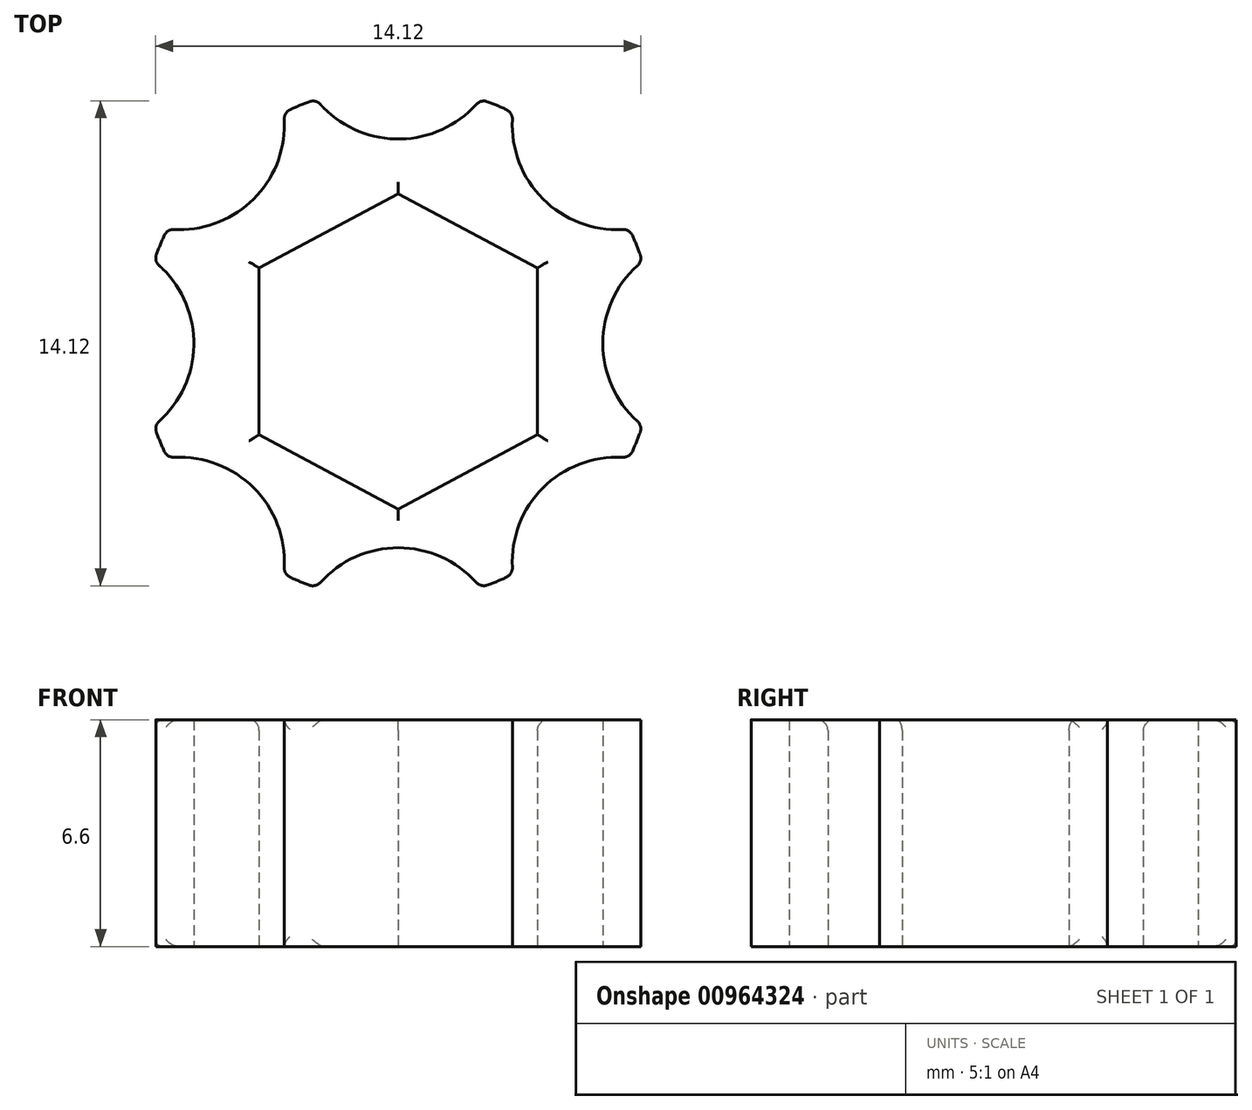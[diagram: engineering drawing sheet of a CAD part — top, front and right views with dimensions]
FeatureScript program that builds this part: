
annotation { "Feature Type Name" : "Feature", "Feature Type Description" : "" }
export const myFeature = defineFeature(function(context is Context, id is Id, definition is map)
    precondition{}
    {
        {
            var Q0;
            Q0=qCreatedBy(makeId("Top.planeOp"),FACE);
            var sketch = newSketch(context, id + "F0", { "sketchPlane" : qUnion([Q0])});
            skLineSegment(sketch, "E0", {"start": v(-4.05, 2.2) * mm, "end": v(-4.05, -2.66) * mm});
            skLineSegment(sketch, "E1", {"start": v(-4.05, -2.66) * mm, "end": v(0, -4.82) * mm});
            skLineSegment(sketch, "E2", {"start": v(0, -4.82) * mm, "end": v(4.05, -2.66) * mm});
            skLineSegment(sketch, "E3", {"start": v(4.05, -2.66) * mm, "end": v(4.05, 2.2) * mm});
            skLineSegment(sketch, "E4", {"start": v(4.05, 2.2) * mm, "end": v(0, 4.36) * mm});
            skLineSegment(sketch, "E5", {"start": v(0, 4.36) * mm, "end": v(-4.05, 2.2) * mm});
            skCircle(sketch, "E6", {"center": v(0, 0) * mm, "radius": 7.5 * mm});
            skLineSegment(sketch, "E7", {"start": v(0, 9) * mm, "end": v(0, 0) * mm, "construction": true});
            skCircle(sketch, "E8", {"center": v(0, 9) * mm, "radius": 3.05 * mm});
            skCircle(sketch, "E9.1.0", {"center": v(-6.36, 6.36) * mm, "radius": 3.05 * mm});
            skCircle(sketch, "E9.2.0", {"center": v(-9, 0) * mm, "radius": 3.05 * mm});
            skCircle(sketch, "E9.3.0", {"center": v(-6.36, -6.36) * mm, "radius": 3.05 * mm});
            skCircle(sketch, "E9.4.0", {"center": v(0, -9) * mm, "radius": 3.05 * mm});
            skCircle(sketch, "E9.5.0", {"center": v(6.36, -6.36) * mm, "radius": 3.05 * mm});
            skCircle(sketch, "E9.6.0", {"center": v(9, 0) * mm, "radius": 3.05 * mm});
            skCircle(sketch, "E9.7.0", {"center": v(6.36, 6.36) * mm, "radius": 3.05 * mm});
            skSolve(sketch);
        }
        {
            var Q0;
            Q0=makeQuery(id+"F0.imprint","IMPRINT",FACE,{"disambiguationData":[TD([[makeQuery(id+"F0.imprint","IMPRINT",EDGE,{"derivedFrom":sQuery(id+"F0.wireOp",EDGE,"E0")}),-1.0]])]});
            extrude(context, id + "F1", {"entities" : qUnion([Q0]), "depth" : 6.6 * mm, "offsetDistance" : 25 * mm});
        }
        {
            var Q0;
            Q0=makeQuery(id+"F1.opExtrude","CAP_EDGE",EDGE,{"disambiguationData":[OSD([sQuery(id+"F0.wireOp",EDGE,"E5")])],"isStart":false});
            var Q1;
            Q1=makeQuery(id+"F1.opExtrude","CAP_EDGE",EDGE,{"disambiguationData":[OSD([sQuery(id+"F0.wireOp",EDGE,"E0")])],"isStart":false});
            var Q2;
            Q2=makeQuery(id+"F1.opExtrude","CAP_EDGE",EDGE,{"disambiguationData":[OSD([sQuery(id+"F0.wireOp",EDGE,"E1")])],"isStart":false});
            var Q3;
            Q3=makeQuery(id+"F1.opExtrude","CAP_EDGE",EDGE,{"disambiguationData":[OSD([sQuery(id+"F0.wireOp",EDGE,"E2")])],"isStart":false});
            var Q4;
            Q4=makeQuery(id+"F1.opExtrude","CAP_EDGE",EDGE,{"disambiguationData":[OSD([sQuery(id+"F0.wireOp",EDGE,"E3")])],"isStart":false});
            var Q5;
            Q5=makeQuery(id+"F1.opExtrude","CAP_EDGE",EDGE,{"disambiguationData":[OSD([sQuery(id+"F0.wireOp",EDGE,"E4")])],"isStart":false});
            var Q6;
            {var subQ0=sQuery(id+"F0.wireOp",EDGE,"E9.7.0");var subQ1=sQuery(id+"F0.wireOp",EDGE,"E6");Q6=makeQuery(id+"F1.opExtrude","SWEPT_EDGE",EDGE,{"disambiguationData":[OSD([subQ1,subQ0]),TDD([makeQuery(id+"F0.imprint","INTERSECT",VERTEX,{"disambiguationData":[OD(1.0)],"derivedFrom":[subQ1,subQ0]})])]});}
            var Q7;
            {var subQ0=sQuery(id+"F0.wireOp",EDGE,"E8");var subQ1=sQuery(id+"F0.wireOp",EDGE,"E6");Q7=makeQuery(id+"F1.opExtrude","SWEPT_EDGE",EDGE,{"disambiguationData":[OSD([subQ1,subQ0]),TDD([makeQuery(id+"F0.imprint","INTERSECT",VERTEX,{"disambiguationData":[OD(0.0)],"derivedFrom":[subQ1,subQ0]})])]});}
            var Q8;
            {var subQ0=sQuery(id+"F0.wireOp",EDGE,"E9.7.0");var subQ1=sQuery(id+"F0.wireOp",EDGE,"E6");Q8=makeQuery(id+"F1.opExtrude","SWEPT_EDGE",EDGE,{"disambiguationData":[OSD([subQ1,subQ0]),TDD([makeQuery(id+"F0.imprint","INTERSECT",VERTEX,{"disambiguationData":[OD(0.0)],"derivedFrom":[subQ1,subQ0]})])]});}
            var Q9;
            {var subQ0=sQuery(id+"F0.wireOp",EDGE,"E9.6.0");var subQ1=sQuery(id+"F0.wireOp",EDGE,"E6");Q9=makeQuery(id+"F1.opExtrude","SWEPT_EDGE",EDGE,{"disambiguationData":[OSD([subQ1,subQ0]),TDD([makeQuery(id+"F0.imprint","INTERSECT",VERTEX,{"disambiguationData":[OD(0.0)],"derivedFrom":[subQ1,subQ0]})])]});}
            var Q10;
            {var subQ0=sQuery(id+"F0.wireOp",EDGE,"E9.6.0");var subQ1=sQuery(id+"F0.wireOp",EDGE,"E6");Q10=makeQuery(id+"F1.opExtrude","SWEPT_EDGE",EDGE,{"disambiguationData":[OSD([subQ1,subQ0]),TDD([makeQuery(id+"F0.imprint","INTERSECT",VERTEX,{"disambiguationData":[OD(1.0)],"derivedFrom":[subQ1,subQ0]})])]});}
            var Q11;
            {var subQ0=sQuery(id+"F0.wireOp",EDGE,"E9.5.0");var subQ1=sQuery(id+"F0.wireOp",EDGE,"E6");Q11=makeQuery(id+"F1.opExtrude","SWEPT_EDGE",EDGE,{"disambiguationData":[OSD([subQ1,subQ0]),TDD([makeQuery(id+"F0.imprint","INTERSECT",VERTEX,{"disambiguationData":[OD(1.0)],"derivedFrom":[subQ1,subQ0]})])]});}
            var Q12;
            {var subQ0=sQuery(id+"F0.wireOp",EDGE,"E9.5.0");var subQ1=sQuery(id+"F0.wireOp",EDGE,"E6");Q12=makeQuery(id+"F1.opExtrude","SWEPT_EDGE",EDGE,{"disambiguationData":[OSD([subQ1,subQ0]),TDD([makeQuery(id+"F0.imprint","INTERSECT",VERTEX,{"disambiguationData":[OD(0.0)],"derivedFrom":[subQ1,subQ0]})])]});}
            var Q13;
            {var subQ0=sQuery(id+"F0.wireOp",EDGE,"E9.4.0");var subQ1=sQuery(id+"F0.wireOp",EDGE,"E6");Q13=makeQuery(id+"F1.opExtrude","SWEPT_EDGE",EDGE,{"disambiguationData":[OSD([subQ1,subQ0]),TDD([makeQuery(id+"F0.imprint","INTERSECT",VERTEX,{"disambiguationData":[OD(1.0)],"derivedFrom":[subQ1,subQ0]})])]});}
            var Q14;
            {var subQ0=sQuery(id+"F0.wireOp",EDGE,"E9.4.0");var subQ1=sQuery(id+"F0.wireOp",EDGE,"E6");Q14=makeQuery(id+"F1.opExtrude","SWEPT_EDGE",EDGE,{"disambiguationData":[OSD([subQ1,subQ0]),TDD([makeQuery(id+"F0.imprint","INTERSECT",VERTEX,{"disambiguationData":[OD(0.0)],"derivedFrom":[subQ1,subQ0]})])]});}
            var Q15;
            {var subQ0=sQuery(id+"F0.wireOp",EDGE,"E9.3.0");var subQ1=sQuery(id+"F0.wireOp",EDGE,"E6");Q15=makeQuery(id+"F1.opExtrude","SWEPT_EDGE",EDGE,{"disambiguationData":[OSD([subQ1,subQ0]),TDD([makeQuery(id+"F0.imprint","INTERSECT",VERTEX,{"disambiguationData":[OD(1.0)],"derivedFrom":[subQ1,subQ0]})])]});}
            var Q16;
            {var subQ0=sQuery(id+"F0.wireOp",EDGE,"E9.3.0");var subQ1=sQuery(id+"F0.wireOp",EDGE,"E6");Q16=makeQuery(id+"F1.opExtrude","SWEPT_EDGE",EDGE,{"disambiguationData":[OSD([subQ1,subQ0]),TDD([makeQuery(id+"F0.imprint","INTERSECT",VERTEX,{"disambiguationData":[OD(0.0)],"derivedFrom":[subQ1,subQ0]})])]});}
            var Q17;
            {var subQ0=sQuery(id+"F0.wireOp",EDGE,"E9.2.0");var subQ1=sQuery(id+"F0.wireOp",EDGE,"E6");Q17=makeQuery(id+"F1.opExtrude","SWEPT_EDGE",EDGE,{"disambiguationData":[OSD([subQ1,subQ0]),TDD([makeQuery(id+"F0.imprint","INTERSECT",VERTEX,{"disambiguationData":[OD(1.0)],"derivedFrom":[subQ1,subQ0]})])]});}
            var Q18;
            {var subQ0=sQuery(id+"F0.wireOp",EDGE,"E6");Q18=makeQuery(id+"F1.opExtrude","SWEPT_FACE",FACE,{"disambiguationData":[OSD([subQ0]),TDD([makeQuery(id+"F0.imprint","IMPRINT",EDGE,{"disambiguationData":[TD([[makeQuery(id+"F0.imprint","INTERSECT",VERTEX,{"disambiguationData":[OD(1.0)],"derivedFrom":[subQ0,sQuery(id+"F0.wireOp",EDGE,"E9.1.0")]}),-1.0]])],"derivedFrom":subQ0})])]});}
            var Q19;
            {var subQ0=sQuery(id+"F0.wireOp",EDGE,"E9.2.0");var subQ1=sQuery(id+"F0.wireOp",EDGE,"E6");Q19=makeQuery(id+"F1.opExtrude","SWEPT_EDGE",EDGE,{"disambiguationData":[OSD([subQ1,subQ0]),TDD([makeQuery(id+"F0.imprint","INTERSECT",VERTEX,{"disambiguationData":[OD(0.0)],"derivedFrom":[subQ1,subQ0]})])]});}
            var Q20;
            {var subQ0=sQuery(id+"F0.wireOp",EDGE,"E6");Q20=makeQuery(id+"F1.opExtrude","SWEPT_FACE",FACE,{"disambiguationData":[OSD([subQ0]),TDD([makeQuery(id+"F0.imprint","IMPRINT",EDGE,{"disambiguationData":[TD([[makeQuery(id+"F0.imprint","INTERSECT",VERTEX,{"disambiguationData":[OD(1.0)],"derivedFrom":[subQ0,sQuery(id+"F0.wireOp",EDGE,"E8")]}),-1.0]])],"derivedFrom":subQ0})])]});}
            fillet(context, id + "F2", {"entities" : qUnion([Q0, Q1, Q2, Q3, Q4, Q5, Q6, Q7, Q8, Q9, Q10, Q11, Q12, Q13, Q14, Q15, Q16, Q17, Q18, Q19, Q20]), "radius" : 0.3 * mm, "tangentPropagation" : true, "allowEdgeOverflow" : false});
        }
    });
